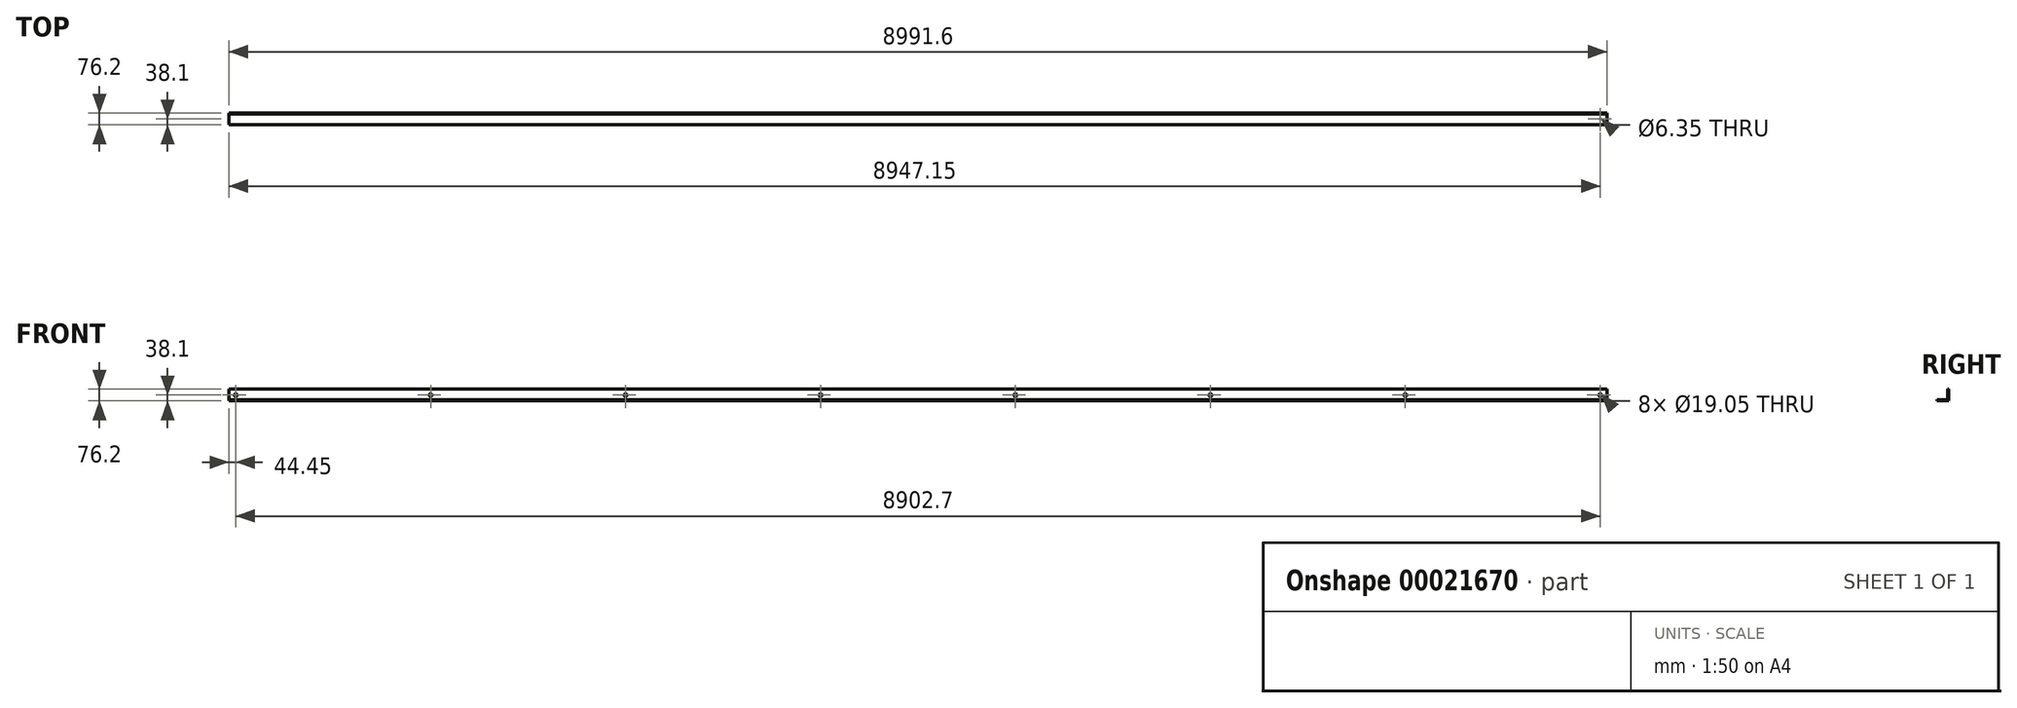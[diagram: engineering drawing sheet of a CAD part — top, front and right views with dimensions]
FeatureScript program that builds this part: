
annotation { "Feature Type Name" : "Feature", "Feature Type Description" : "" }
export const myFeature = defineFeature(function(context is Context, id is Id, definition is map)
    precondition{}
    {
        {
            var Q0;
            Q0=qCreatedBy(makeId("Right.planeOp"),FACE);
            var sketch = newSketch(context, id + "F0", { "sketchPlane" : qUnion([Q0])});
            skLineSegment(sketch, "E0", {"start": v(0, 0) * mm, "end": v(0, 76.2) * mm});
            skLineSegment(sketch, "E1", {"start": v(0, 76.2) * mm, "end": v(-6.35, 76.2) * mm});
            skLineSegment(sketch, "E2", {"start": v(-6.35, 76.2) * mm, "end": v(-6.35, 6.35) * mm});
            skLineSegment(sketch, "E3", {"start": v(-6.35, 6.35) * mm, "end": v(-76.2, 6.35) * mm});
            skLineSegment(sketch, "E4", {"start": v(-76.2, 6.35) * mm, "end": v(-76.2, 0) * mm});
            skLineSegment(sketch, "E5", {"start": v(-76.2, 0) * mm, "end": v(0, 0) * mm});
            skSolve(sketch);
        }
        {
            var Q0;
            Q0=makeQuery(id+"F0.imprint","IMPRINT",FACE,{"disambiguationData":[TD([[makeQuery(id+"F0.imprint","IMPRINT",EDGE,{"derivedFrom":sQuery(id+"F0.wireOp",EDGE,"E0")}),1.0]])]});
            extrude(context, id + "F1", {"entities" : qUnion([Q0]), "depth" : 8991.6 * mm});
        }
        {
            var Q0;
            Q0=makeQuery(id+"F1.opExtrude","SWEPT_FACE",FACE,{"disambiguationData":[OSD([sQuery(id+"F0.wireOp",EDGE,"E5")])]});
            var sketch = newSketch(context, id + "F2", { "sketchPlane" : qUnion([Q0])});
            skLineSegment(sketch, "E6", {"start": v(0, 38.1) * mm, "end": v(44.45, 38.1) * mm, "construction": true});
            skLineSegment(sketch, "E7", {"start": v(0, 38.1) * mm, "end": v(1524, 38.1) * mm, "construction": true});
            skCircle(sketch, "E8", {"center": v(44.45, 38.1) * mm, "radius": 9.53 * mm});
            skCircle(sketch, "E9", {"center": v(1524, 38.1) * mm, "radius": 9.53 * mm});
            skCircle(sketch, "E10.1.0.0", {"center": v(3352.8, 38.1) * mm, "radius": 9.53 * mm});
            skLineSegment(sketch, "E10.direction1", {"start": v(1524, 38.1) * mm, "end": v(3352.8, 38.1) * mm, "construction": true});
            skCircle(sketch, "E11.0.2.0", {"center": v(5181.6, 38.1) * mm, "radius": 9.53 * mm});
            skCircle(sketch, "E11.0.3.0", {"center": v(7010.4, 38.1) * mm, "radius": 9.53 * mm});
            skLineSegment(sketch, "E12", {"start": v(8991.6, 38.1) * mm, "end": v(8947.15, 38.1) * mm, "construction": true});
            skCircle(sketch, "E13", {"center": v(8947.15, 38.1) * mm, "radius": 9.53 * mm});
            skSolve(sketch);
        }
        {
            var Q0;
            Q0=sQuery(id+"F2.wireOp",VERTEX,"E13.center");
            var Q1;
            Q1=makeQuery(id+"F1.opExtrude","SWEPT_BODY",BODY,{"disambiguationData":[OSD([sQuery(id+"F0.wireOp",EDGE,"E0"),sQuery(id+"F0.wireOp",EDGE,"E1"),sQuery(id+"F0.wireOp",EDGE,"E2"),sQuery(id+"F0.wireOp",EDGE,"E3"),sQuery(id+"F0.wireOp",EDGE,"E4"),sQuery(id+"F0.wireOp",EDGE,"E5")])]});
            hole(context, id + "F3", {"style" : HoleStyle.SIMPLE, "endStyle" : HoleEndStyle.THROUGH, "holeDiameter" : 6.35 * mm, "locations" : qUnion([Q0]), "scope" : qUnion([Q1]), "isTappedThrough" : true, "startStyle" : HoleStartStyle.PART});
        }
        {
            var Q0;
            Q0=makeQuery(id+"F1.opExtrude","SWEPT_FACE",FACE,{"disambiguationData":[OSD([sQuery(id+"F0.wireOp",EDGE,"E0")])]});
            var sketch = newSketch(context, id + "F4", { "sketchPlane" : qUnion([Q0])});
            skLineSegment(sketch, "E14", {"start": v(-8991.6, 38.1) * mm, "end": v(-8947.15, 38.1) * mm, "construction": true});
            skCircle(sketch, "E15", {"center": v(-8947.15, 38.1) * mm, "radius": 9.53 * mm});
            skCircle(sketch, "E16.1.0.0", {"center": v(-7675.35, 38.1) * mm, "radius": 9.53 * mm});
            skCircle(sketch, "E16.2.0.0", {"center": v(-6403.54, 38.1) * mm, "radius": 9.53 * mm});
            skCircle(sketch, "E16.3.0.0", {"center": v(-5131.74, 38.1) * mm, "radius": 9.53 * mm});
            skLineSegment(sketch, "E16.direction1", {"start": v(-8947.15, 38.1) * mm, "end": v(-7675.35, 38.1) * mm, "construction": true});
            skLineSegment(sketch, "E17", {"start": v(0, 38.1) * mm, "end": v(-44.45, 38.1) * mm, "construction": true});
            skCircle(sketch, "E18.0.4.0", {"center": v(-3859.94, 38.1) * mm, "radius": 9.53 * mm});
            skCircle(sketch, "E18.0.5.0", {"center": v(-2588.13, 38.1) * mm, "radius": 9.53 * mm});
            skCircle(sketch, "E19.0.6.0", {"center": v(-1316.33, 38.1) * mm, "radius": 9.53 * mm});
            skSolve(sketch);
        }
        {
            var Q0;
            Q0=sQuery(id+"F4.wireOp",VERTEX,"E15.center");
            var Q1;
            Q1=sQuery(id+"F4.wireOp",VERTEX,"E16.1.0.0.center");
            var Q2;
            Q2=sQuery(id+"F4.wireOp",VERTEX,"E16.2.0.0.center");
            var Q3;
            Q3=sQuery(id+"F4.wireOp",VERTEX,"E16.3.0.0.center");
            var Q4;
            Q4=sQuery(id+"F4.wireOp",VERTEX,"E18.0.4.0.center");
            var Q5;
            Q5=sQuery(id+"F4.wireOp",VERTEX,"E18.0.5.0.center");
            var Q6;
            Q6=sQuery(id+"F4.wireOp",VERTEX,"E19.0.6.0.center");
            var Q7;
            Q7=sQuery(id+"F4.wireOp",VERTEX,"E19.0.7.0.center");
            var Q8;
            Q8=sQuery(id+"F4.wireOp",VERTEX,"E17.end");
            var Q9;
            Q9=makeQuery(id+"F1.opExtrude","SWEPT_BODY",BODY,{"disambiguationData":[OSD([sQuery(id+"F0.wireOp",EDGE,"E0"),sQuery(id+"F0.wireOp",EDGE,"E1"),sQuery(id+"F0.wireOp",EDGE,"E2"),sQuery(id+"F0.wireOp",EDGE,"E3"),sQuery(id+"F0.wireOp",EDGE,"E4"),sQuery(id+"F0.wireOp",EDGE,"E5")])]});
            hole(context, id + "F5", {"style" : HoleStyle.SIMPLE, "endStyle" : HoleEndStyle.THROUGH, "holeDiameter" : 19.05 * mm, "locations" : qUnion([Q0, Q1, Q2, Q3, Q4, Q5, Q6, Q7, Q8]), "scope" : qUnion([Q9]), "isTappedThrough" : true, "startStyle" : HoleStartStyle.PART});
        }
    });
